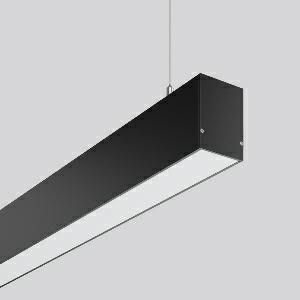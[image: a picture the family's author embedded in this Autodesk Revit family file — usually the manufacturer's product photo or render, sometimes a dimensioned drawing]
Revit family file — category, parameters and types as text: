
# Revit family: less_is_more_50_312321_003_76_7aea
name_source: partatom
category: Lighting Fixtures
units: mm (PartAtom-declared; Revit-internal decimal feet)

## family parameters
Cut with Voids When Loaded = No
Host = Face
Light Source = No
Part Type = Normal
Room Calculation Point = No
Round Connector Dimension = Use Diameter
Shared = No

## types (1)
- LESS IS MORE 50 (1 x LED Modul 830, 8450 lm, 3000)
    Apparent Load = 74 VA
    CIE Flux Codes = 49 80 96 63 100
    Color Rendering = 80
    Color Temperature = 3000
    Default Elevation = 1800 mm
    Description = Series: LESS IS MORE 50
Linear pendant luminaire for aesthetically sophisticated lighting. Housing: extruded aluminium profile, powder-coated. End cap aluminium powder-coated. Canopy made of aluminium, powder-coated. Diffuser made of non-yellowing plastic (PMMA), opal. Direct 65%, indirect 35% light emission. Controlled separately. Suitable for pendant. 2-point steel cable suspension freely positionable and infinitely height-adjustable. Special lengths available on request. LED unit with integrated converter interchangeable and removable. Suitable for through-wiring. With sensors or as a safety luminaire on request. 
Colour: deep black, matt (RAL 9005)
Length: 1967 mm
Width: 57 mm
Height: 75 mm
Suspension length: 2000 mm
Lamp: LED
Socket: without socket
Colour temperature: 3000K
Colour rendering index (CRI): 80
Light source: LED
Socket lamp2: Without base
Colour temperature: 3000K
System power: 74 W
Rated luminous flux: 8450 lm
Luminous efficiency: 114 lm/W
Control gear: Converter, dimmable, DALI
Control gear: Converter, dimmable, DALI
Protection class: I
Type of protection: IP 20
    Height = 75 mm
    Lamp = 1 x LED Modul 830
    Lamp Light Flux = 8450 lm
    Lamp count = 1
    Length = 1967 mm
    Lifetime = 50000 h
    Luminous efficacy = 114 lm/W
    Manufacturer = RZB
    ModVariant = No
    Model = 312321.003.76
    Mounting Place = Ceiling
    Mounting Type = Pendant
    Number of Poles = 1
    OnlyDefault = Yes
    Power Factor = 1
    Product Name = LESS IS MORE 50
    Product group = Pendant LED linear luminaires
    ProductGroupID = 907
    Protection Class = Protection class I
    Protection Degree = IP 20
    RLX_Detail_Level = 1
    RLX_Emergency_Light_Flux = 0 lm
    RLX_Emergency_Type = 0
    RLX_Emergency_Type_DB = No
    RlxData = <blob elided: 39889 chars, md5=9fb702e5>
    Socket = socket
    Standby Power = 0 W
    System Light Flux = 8450 lm
    System Power = 74 W
    Type Comments = Product without accessories
    Type Image = 312318.003.jpg
    URL = http://relux.com
    VarID = ---
    Voltage = 230 V
    Voltage Range = 220-240 V
    Weight = 0.00 kg
    Width = 57 mm

## geometry (parser evidence)
native form markers: Blend x4, Sweep x13
no freeform markers — native parametric forms only
